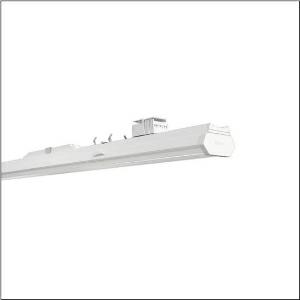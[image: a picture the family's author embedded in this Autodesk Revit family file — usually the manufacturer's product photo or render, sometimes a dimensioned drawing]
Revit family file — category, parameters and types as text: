
# Revit family: licross_r__21_protected_ho_52td1bdn4d5m_ff94
name_source: partatom
category: Lighting Fixtures
units: mm (PartAtom-declared; Revit-internal decimal feet)

## family parameters
Cut with Voids When Loaded = No
Host = Face
Light Source = No
Part Type = Normal
Room Calculation Point = No
Round Connector Dimension = Use Diameter
Shared = No

## types (1)
- --- (1 x LED, 13950 lm, 84.9 W, 4000K)
    Apparent Load = 85 VA
    CIE Flux Codes = 54 82 95 97 100
    Color Rendering = 80
    Color Temperature = 4000K
    Default Elevation = 1800 mm
    Description = Licross® 21 Protected HO, luminaire insert, of sheet steel, galvanised, coil coated, white, length: 1.500mm, width: 90mm, height: 103mm, LED rated luminous flux: 13.950lm, light colour: 840, control gear: DALI 2, with plug, 5-pole, with phase selection, mains connection: 220..240V, AC, 50/60Hz, rated input power: 85W, internal wiring halogen-free, primary optical cover: cover, of PMMA, light emission: direct distribution, primary light characteristic: symmetric, protection rating (complete): IP54, insulation class (complete): insulation class I (protective earthing), certification: CE, ENEC, VDE, UKCA, protection symbol: D if used in an environment with non-conductive dust loads with corresponding accessories, impact resistance: IK06, permissible ambient temperature for indoor applications: -25..+35°C, corresponds to IFS (International Featured Standards) requirements for safety and quality in the food industry, reducing of maximum allowable ambient temperature of 5°C with ceiling mounting, LABS conformity tested according to VDMA 24364:2018-05, packaging unit: 1 piece
    Height = 92 mm
    Lamp = 1 x LED
    Lamp Light Flux = 13950 lm
    Lamp Power = 84.9 W
    Lamp count = 1
    Length = 1500 mm
    Luminous efficacy = 164 lm/W
    Manufacturer = Siteco
    ModVariant = No
    Model = 52TD1BDN4D5M
    Mounting Place = Ceiling
    Mounting Type = Pendant
    Number of Poles = 1
    OnlyDefault = Yes
    Power Factor = 1
    Product Name = Licross® 21 Protected HO
    Product group = luminaire insert | ceiling pendant
    ProductGroupID = 902
    Protection Class = Protection class I
    Protection Degree = IP 54
    RLX_Detail_Level = 1
    RLX_Emergency_Light_Flux = 0 lm
    RLX_Emergency_Type = 0
    RLX_Emergency_Type_DB = No
    RlxData = <blob elided: 24277 chars, md5=dd023d40>
    Socket = socket
    Standby Power = 0 W
    System Light Flux = 13950 lm
    System Power = 85 W
    Type Comments = factory setting: luminous flux: 100 % | dim-lin: 254 | 484 mA
    Type Image = l_1256148.jpg
    URL = http://relux.com
    VarID = @adj_150617
    Voltage = 0 V
    Weight = 0.00 kg
    Width = 88 mm

## geometry (parser evidence)
native form markers: Blend x4, Sweep x11
no freeform markers — native parametric forms only
